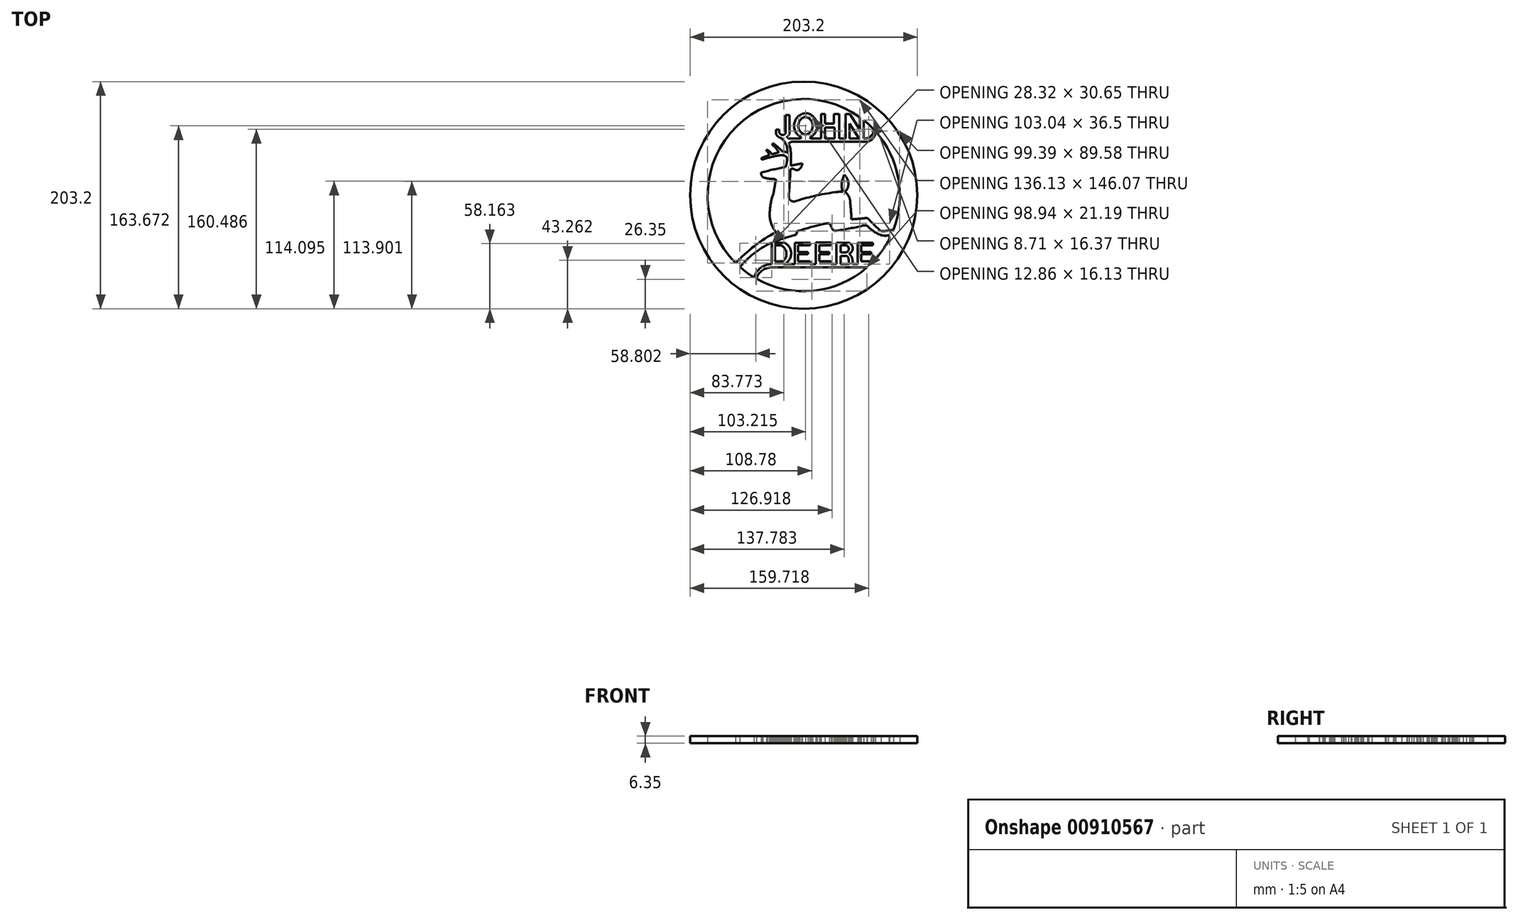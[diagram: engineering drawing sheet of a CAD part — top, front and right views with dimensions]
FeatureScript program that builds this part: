
annotation { "Feature Type Name" : "Feature", "Feature Type Description" : "" }
export const myFeature = defineFeature(function(context is Context, id is Id, definition is map)
    precondition{}
    {
        {
            var Q0;
            Q0=qCreatedBy(makeId("Top.planeOp"),FACE);
            var sketch = newSketch(context, id + "F0", { "sketchPlane" : qUnion([Q0])});
            skCircle(sketch, "E0", {"center": v(101.6, 101.6) * mm, "radius": 101.6 * mm});
            skPoint(sketch, "E0.centerSnap0", {"position": v(0, 101.6) * mm});
            skPoint(sketch, "E0.centerSnap1", {"position": v(101.6, 0) * mm});
            skCircle(sketch, "E1", {"center": v(101.6, 101.6) * mm, "radius": 85.96 * mm});
            skArc(sketch, "E2", {"start": v(76.83, 68.48) * mm, "mid": v(57.67, 56.15) * mm, "end": v(40.77, 40.87) * mm});
            skArc(sketch, "E3", {"start": v(71.8, 58.56) * mm, "mid": v(57.04, 49.4) * mm, "end": v(44.64, 37.22) * mm});
            skArc(sketch, "E4", {"start": v(94.74, 66.06) * mm, "mid": v(86.2, 63.73) * mm, "end": v(77.86, 60.78) * mm});
            skArc(sketch, "E5", {"start": v(71.2, 84.1) * mm, "mid": v(72.6, 75.78) * mm, "end": v(76.83, 68.48) * mm});
            skArc(sketch, "E6", {"start": v(74.65, 103.27) * mm, "mid": v(72.06, 93.84) * mm, "end": v(71.2, 84.1) * mm});
            skArc(sketch, "E7", {"start": v(76.83, 115.22) * mm, "mid": v(75.65, 109.26) * mm, "end": v(74.65, 103.27) * mm});
            skArc(sketch, "E8", {"start": v(76.83, 115.22) * mm, "mid": v(75.85, 115.9) * mm, "end": v(74.65, 115.9) * mm});
            skArc(sketch, "E9", {"start": v(65.1, 117.6) * mm, "mid": v(69.81, 116.4) * mm, "end": v(74.65, 115.9) * mm});
            skArc(sketch, "E10", {"start": v(63.55, 121.74) * mm, "mid": v(63.88, 119.5) * mm, "end": v(65.1, 117.6) * mm});
            skArc(sketch, "E11", {"start": v(85.15, 126.7) * mm, "mid": v(74.28, 124.5) * mm, "end": v(63.55, 121.74) * mm});
            skArc(sketch, "E12", {"start": v(85.15, 126.7) * mm, "mid": v(86.52, 130.95) * mm, "end": v(86.51, 135.41) * mm});
            skArc(sketch, "E13", {"start": v(86.51, 135.41) * mm, "mid": v(83.76, 137.18) * mm, "end": v(80.5, 137.28) * mm});
            skArc(sketch, "E14", {"start": v(80.5, 137.28) * mm, "mid": v(72.72, 135.77) * mm, "end": v(65.1, 133.59) * mm});
            skArc(sketch, "E15", {"start": v(70.75, 137.28) * mm, "mid": v(67.41, 136.16) * mm, "end": v(64.14, 134.86) * mm});
            skArc(sketch, "E16", {"start": v(79.18, 139.83) * mm, "mid": v(76.2, 139.04) * mm, "end": v(73.25, 138.1) * mm});
            skArc(sketch, "E17", {"start": v(87.29, 139.6) * mm, "mid": v(84.96, 140.45) * mm, "end": v(82.5, 140.74) * mm});
            skArc(sketch, "E18", {"start": v(70.75, 137.28) * mm, "mid": v(69.91, 139.5) * mm, "end": v(68.24, 141.2) * mm});
            skArc(sketch, "E19", {"start": v(73.25, 138.1) * mm, "mid": v(71.5, 140.27) * mm, "end": v(69.33, 142.02) * mm});
            skArc(sketch, "E20", {"start": v(79.18, 139.83) * mm, "mid": v(76.9, 143.39) * mm, "end": v(73.94, 146.4) * mm});
            skArc(sketch, "E21", {"start": v(82.5, 140.74) * mm, "mid": v(78.7, 144.39) * mm, "end": v(74.65, 147.76) * mm});
            skArc(sketch, "E22", {"start": v(87.29, 139.6) * mm, "mid": v(85.92, 146.82) * mm, "end": v(81.55, 152.73) * mm});
            skArc(sketch, "E23", {"start": v(90.07, 139.01) * mm, "mid": v(88.79, 146.15) * mm, "end": v(84.7, 152.14) * mm});
            skArc(sketch, "E24", {"start": v(90.07, 127.98) * mm, "mid": v(90.2, 133.5) * mm, "end": v(90.07, 139.01) * mm});
            skArc(sketch, "E25", {"start": v(100.32, 129.94) * mm, "mid": v(95.18, 129.07) * mm, "end": v(90.07, 127.98) * mm});
            skArc(sketch, "E26", {"start": v(96.77, 124.1) * mm, "mid": v(99.29, 126.57) * mm, "end": v(100.32, 129.94) * mm});
            skArc(sketch, "E27", {"start": v(92.71, 125.02) * mm, "mid": v(94.64, 124.13) * mm, "end": v(96.77, 124.1) * mm});
            skArc(sketch, "E28", {"start": v(92.71, 125.02) * mm, "mid": v(91.1, 125.2) * mm, "end": v(89.63, 124.49) * mm});
            skArc(sketch, "E29", {"start": v(88.5, 104.49) * mm, "mid": v(89.22, 114.48) * mm, "end": v(89.63, 124.49) * mm});
            skArc(sketch, "E30", {"start": v(88.5, 104.49) * mm, "mid": v(88.4, 101.57) * mm, "end": v(88.5, 98.65) * mm});
            skArc(sketch, "E31", {"start": v(88.5, 98.65) * mm, "mid": v(91.3, 96.14) * mm, "end": v(95.06, 96.47) * mm});
            skArc(sketch, "E32", {"start": v(131.98, 104.49) * mm, "mid": v(113.33, 101.34) * mm, "end": v(95.06, 96.47) * mm});
            skArc(sketch, "E33", {"start": v(136.48, 104.79) * mm, "mid": v(134.23, 104.64) * mm, "end": v(131.98, 104.49) * mm});
            skArc(sketch, "E34", {"start": v(137.93, 119.83) * mm, "mid": v(135.67, 112.45) * mm, "end": v(136.48, 104.79) * mm});
            skArc(sketch, "E35", {"start": v(141.53, 110.71) * mm, "mid": v(140.82, 115.7) * mm, "end": v(137.93, 119.83) * mm});
            skArc(sketch, "E36", {"start": v(139.3, 105.52) * mm, "mid": v(140.85, 107.93) * mm, "end": v(141.53, 110.71) * mm});
            skArc(sketch, "E37", {"start": v(139.3, 105.52) * mm, "mid": v(139.23, 104.3) * mm, "end": v(139.89, 103.27) * mm});
            skArc(sketch, "E38", {"start": v(143.09, 96.97) * mm, "mid": v(142.03, 100.4) * mm, "end": v(139.89, 103.27) * mm});
            skArc(sketch, "E39", {"start": v(144.4, 79.99) * mm, "mid": v(143.82, 88.49) * mm, "end": v(143.09, 96.97) * mm});
            skArc(sketch, "E40", {"start": v(144.4, 79.99) * mm, "mid": v(151.45, 80.46) * mm, "end": v(158.46, 81.3) * mm});
            skArc(sketch, "E41", {"start": v(158.46, 81.3) * mm, "mid": v(164.51, 75.18) * mm, "end": v(170.8, 69.3) * mm});
            skArc(sketch, "E42", {"start": v(170.8, 69.3) * mm, "mid": v(173.77, 69.49) * mm, "end": v(176.72, 69.88) * mm});
            skArc(sketch, "E43", {"start": v(168.8, 66.67) * mm, "mid": v(173.2, 65.44) * mm, "end": v(177.75, 65.63) * mm});
            skArc(sketch, "E44", {"start": v(158.46, 74.3) * mm, "mid": v(163.23, 69.94) * mm, "end": v(168.8, 66.67) * mm});
            skArc(sketch, "E45", {"start": v(158.46, 74.3) * mm, "mid": v(155.8, 74.57) * mm, "end": v(153.2, 73.99) * mm});
            skArc(sketch, "E46", {"start": v(129.98, 69.6) * mm, "mid": v(141.64, 71.56) * mm, "end": v(153.2, 73.99) * mm});
            skArc(sketch, "E47", {"start": v(126.93, 72.05) * mm, "mid": v(128.02, 70.28) * mm, "end": v(129.98, 69.6) * mm});
            skArc(sketch, "E48", {"start": v(124.63, 76.41) * mm, "mid": v(125.76, 74.22) * mm, "end": v(126.93, 72.05) * mm});
            skArc(sketch, "E49", {"start": v(124.63, 76.41) * mm, "mid": v(120.53, 76.1) * mm, "end": v(116.54, 75.15) * mm});
            skArc(sketch, "E50", {"start": v(116.54, 75.15) * mm, "mid": v(106.19, 72.38) * mm, "end": v(95.92, 69.3) * mm});
            skLineSegment(sketch, "E51", {"start": v(95.92, 69.3) * mm, "end": v(94.74, 66.06) * mm});
            skArc(sketch, "E52", {"start": v(64.14, 134.86) * mm, "mid": v(64.08, 133.82) * mm, "end": v(65.1, 133.59) * mm});
            skArc(sketch, "E53", {"start": v(69.33, 142.02) * mm, "mid": v(68.46, 142.05) * mm, "end": v(68.24, 141.2) * mm});
            skArc(sketch, "E54", {"start": v(74.65, 147.76) * mm, "mid": v(73.79, 147.34) * mm, "end": v(73.94, 146.4) * mm});
            skLineSegment(sketch, "E55", {"start": v(72.96, 58.59) * mm, "end": v(72.96, 39.91) * mm});
            skLineSegment(sketch, "E56", {"start": v(72.96, 39.91) * mm, "end": v(84.43, 39.91) * mm});
            skLineSegment(sketch, "E57", {"start": v(75.4, 59.05) * mm, "end": v(84.3, 59.05) * mm});
            skLineSegment(sketch, "E58", {"start": v(75.92, 56.7) * mm, "end": v(75.92, 42.28) * mm});
            skLineSegment(sketch, "E59", {"start": v(75.92, 42.28) * mm, "end": v(83.2, 42.28) * mm});
            skLineSegment(sketch, "E60", {"start": v(75.92, 56.7) * mm, "end": v(81.54, 56.7) * mm});
            skLineSegment(sketch, "E61", {"start": v(93.6, 59.05) * mm, "end": v(93.6, 39.91) * mm});
            skLineSegment(sketch, "E62", {"start": v(93.6, 39.91) * mm, "end": v(161.47, 39.91) * mm});
            skLineSegment(sketch, "E63", {"start": v(93.6, 59.05) * mm, "end": v(107.18, 59.05) * mm});
            skLineSegment(sketch, "E64", {"start": v(107.18, 59.05) * mm, "end": v(107.18, 56.8) * mm});
            skLineSegment(sketch, "E65", {"start": v(107.18, 56.8) * mm, "end": v(96.62, 56.8) * mm});
            skLineSegment(sketch, "E66", {"start": v(96.62, 56.8) * mm, "end": v(96.62, 50.66) * mm});
            skLineSegment(sketch, "E67", {"start": v(96.62, 50.66) * mm, "end": v(105.52, 50.66) * mm});
            skLineSegment(sketch, "E68", {"start": v(105.52, 50.66) * mm, "end": v(105.52, 48.65) * mm});
            skLineSegment(sketch, "E69", {"start": v(105.52, 48.65) * mm, "end": v(96.62, 48.65) * mm});
            skLineSegment(sketch, "E70", {"start": v(96.62, 48.65) * mm, "end": v(96.62, 42.27) * mm});
            skLineSegment(sketch, "E71", {"start": v(96.62, 42.27) * mm, "end": v(107.18, 42.27) * mm});
            skLineSegment(sketch, "E72", {"start": v(107.18, 42.27) * mm, "end": v(107.18, 39.91) * mm});
            skLineSegment(sketch, "E73", {"start": v(112.5, 59.11) * mm, "end": v(112.5, 39.91) * mm});
            skLineSegment(sketch, "E74", {"start": v(112.5, 59.11) * mm, "end": v(126.08, 59.11) * mm});
            skLineSegment(sketch, "E75", {"start": v(126.08, 59.11) * mm, "end": v(126.08, 56.87) * mm});
            skLineSegment(sketch, "E76", {"start": v(126.08, 56.87) * mm, "end": v(115.52, 56.87) * mm});
            skLineSegment(sketch, "E77", {"start": v(115.52, 56.87) * mm, "end": v(115.52, 50.72) * mm});
            skLineSegment(sketch, "E78", {"start": v(115.52, 50.72) * mm, "end": v(124.42, 50.72) * mm});
            skLineSegment(sketch, "E79", {"start": v(124.42, 50.72) * mm, "end": v(124.42, 48.71) * mm});
            skLineSegment(sketch, "E80", {"start": v(124.42, 48.71) * mm, "end": v(115.52, 48.71) * mm});
            skLineSegment(sketch, "E81", {"start": v(115.52, 48.71) * mm, "end": v(115.52, 42.34) * mm});
            skLineSegment(sketch, "E82", {"start": v(115.52, 42.34) * mm, "end": v(126.08, 42.34) * mm});
            skLineSegment(sketch, "E83", {"start": v(126.08, 42.34) * mm, "end": v(126.08, 39.91) * mm});
            skLineSegment(sketch, "E84", {"start": v(149.94, 59.05) * mm, "end": v(149.94, 39.91) * mm});
            skLineSegment(sketch, "E85", {"start": v(149.94, 59.05) * mm, "end": v(163.52, 59.05) * mm});
            skLineSegment(sketch, "E86", {"start": v(163.52, 59.05) * mm, "end": v(163.52, 56.8) * mm});
            skLineSegment(sketch, "E87", {"start": v(163.52, 56.8) * mm, "end": v(152.96, 56.8) * mm});
            skLineSegment(sketch, "E88", {"start": v(152.96, 56.8) * mm, "end": v(152.96, 50.66) * mm});
            skLineSegment(sketch, "E89", {"start": v(152.96, 50.66) * mm, "end": v(161.86, 50.66) * mm});
            skLineSegment(sketch, "E90", {"start": v(161.86, 50.66) * mm, "end": v(161.86, 48.65) * mm});
            skLineSegment(sketch, "E91", {"start": v(161.86, 48.65) * mm, "end": v(152.96, 48.65) * mm});
            skLineSegment(sketch, "E92", {"start": v(152.96, 48.65) * mm, "end": v(152.96, 42.27) * mm});
            skLineSegment(sketch, "E93", {"start": v(152.96, 42.27) * mm, "end": v(163.52, 42.27) * mm});
            skLineSegment(sketch, "E94", {"start": v(163.52, 42.27) * mm, "end": v(163.52, 39.91) * mm});
            skLineSegment(sketch, "E95", {"start": v(130.76, 39.91) * mm, "end": v(130.76, 59.08) * mm});
            skLineSegment(sketch, "E96", {"start": v(130.76, 59.08) * mm, "end": v(141.44, 59.08) * mm});
            skLineSegment(sketch, "E97", {"start": v(134.77, 39.91) * mm, "end": v(134.77, 47.25) * mm});
            skLineSegment(sketch, "E98", {"start": v(134.77, 47.25) * mm, "end": v(139.02, 47.25) * mm});
            skLineSegment(sketch, "E99", {"start": v(134.77, 50.52) * mm, "end": v(134.77, 56.72) * mm});
            skLineSegment(sketch, "E100", {"start": v(134.77, 56.72) * mm, "end": v(139.83, 56.72) * mm});
            skLineSegment(sketch, "E101", {"start": v(134.77, 50.52) * mm, "end": v(138.9, 50.52) * mm});
            skArc(sketch, "E102", {"start": v(139.83, 50.46) * mm, "mid": v(141.92, 53.6) * mm, "end": v(139.83, 56.72) * mm});
            skArc(sketch, "E103", {"start": v(142.24, 49.2) * mm, "mid": v(145.47, 54.43) * mm, "end": v(141.44, 59.08) * mm});
            skArc(sketch, "E104", {"start": v(144.7, 45.93) * mm, "mid": v(143.63, 47.68) * mm, "end": v(142.24, 49.2) * mm});
            skArc(sketch, "E105", {"start": v(145.45, 39.91) * mm, "mid": v(145.34, 42.95) * mm, "end": v(144.7, 45.93) * mm});
            skArc(sketch, "E106", {"start": v(142.24, 39.91) * mm, "mid": v(141.98, 42.94) * mm, "end": v(141.44, 45.93) * mm});
            skArc(sketch, "E107", {"start": v(141.44, 45.93) * mm, "mid": v(140.4, 46.9) * mm, "end": v(139.02, 47.25) * mm});
            skArc(sketch, "E108", {"start": v(83.2, 42.28) * mm, "mid": v(86.15, 49.93) * mm, "end": v(81.54, 56.7) * mm});
            skArc(sketch, "E109", {"start": v(84.43, 39.91) * mm, "mid": v(90.4, 49.52) * mm, "end": v(84.3, 59.05) * mm});
            skLineSegment(sketch, "E110", {"start": v(138.9, 50.52) * mm, "end": v(139.83, 50.46) * mm});
            skLineSegment(sketch, "E111", {"start": v(85.53, 173.38) * mm, "end": v(88.86, 173.38) * mm});
            skLineSegment(sketch, "E112", {"start": v(88.86, 173.38) * mm, "end": v(88.86, 156.67) * mm});
            skLineSegment(sketch, "E113", {"start": v(85.53, 173.38) * mm, "end": v(85.53, 157.17) * mm});
            skLineSegment(sketch, "E114", {"start": v(76.78, 160.28) * mm, "end": v(79.6, 160.28) * mm});
            skLineSegment(sketch, "E115", {"start": v(79.6, 160.28) * mm, "end": v(79.6, 158.04) * mm});
            skLineSegment(sketch, "E116", {"start": v(76.78, 160.28) * mm, "end": v(76.78, 156.45) * mm});
            skArc(sketch, "E117", {"start": v(76.78, 156.45) * mm, "mid": v(78.71, 154) * mm, "end": v(81.55, 152.73) * mm});
            skArc(sketch, "E118", {"start": v(79.6, 158.04) * mm, "mid": v(82.26, 155.51) * mm, "end": v(85.53, 157.17) * mm});
            skArc(sketch, "E119", {"start": v(103.14, 175.02) * mm, "mid": v(92.98, 163.59) * mm, "end": v(103.23, 152.23) * mm});
            skArc(sketch, "E120", {"start": v(103.23, 152.23) * mm, "mid": v(113.75, 163.67) * mm, "end": v(103.14, 175.02) * mm});
            skArc(sketch, "E121", {"start": v(103.23, 171.74) * mm, "mid": v(96.79, 163.67) * mm, "end": v(103.23, 155.6) * mm});
            skArc(sketch, "E122", {"start": v(103.23, 155.6) * mm, "mid": v(109.64, 163.67) * mm, "end": v(103.23, 171.74) * mm});
            skLineSegment(sketch, "E123", {"start": v(84.7, 152.14) * mm, "end": v(155.36, 152.38) * mm});
            skLineSegment(sketch, "E124", {"start": v(155.36, 152.38) * mm, "end": v(155.36, 168.67) * mm});
            skLineSegment(sketch, "E125", {"start": v(151.84, 171.35) * mm, "end": v(151.84, 160.16) * mm});
            skLineSegment(sketch, "E126", {"start": v(151.84, 160.16) * mm, "end": v(142.97, 174.1) * mm});
            skLineSegment(sketch, "E127", {"start": v(142.97, 174.1) * mm, "end": v(138.96, 174.1) * mm});
            skLineSegment(sketch, "E128", {"start": v(138.96, 174.1) * mm, "end": v(138.96, 152.32) * mm});
            skLineSegment(sketch, "E129", {"start": v(142.6, 152.34) * mm, "end": v(142.56, 165.63) * mm});
            skLineSegment(sketch, "E130", {"start": v(142.56, 165.63) * mm, "end": v(151.26, 152.37) * mm});
            skLineSegment(sketch, "E131", {"start": v(117.18, 152.25) * mm, "end": v(117.1, 174.2) * mm});
            skLineSegment(sketch, "E132", {"start": v(117.1, 174.2) * mm, "end": v(120.73, 174.21) * mm});
            skLineSegment(sketch, "E133", {"start": v(120.73, 174.21) * mm, "end": v(120.76, 165.63) * mm});
            skLineSegment(sketch, "E134", {"start": v(120.76, 165.63) * mm, "end": v(128.75, 165.66) * mm});
            skLineSegment(sketch, "E135", {"start": v(128.75, 165.66) * mm, "end": v(128.75, 174.21) * mm});
            skLineSegment(sketch, "E136", {"start": v(128.75, 174.21) * mm, "end": v(133.4, 174.23) * mm});
            skLineSegment(sketch, "E137", {"start": v(133.4, 174.23) * mm, "end": v(133.47, 152.3) * mm});
            skLineSegment(sketch, "E138", {"start": v(129.3, 152.3) * mm, "end": v(129.3, 162.26) * mm});
            skLineSegment(sketch, "E139", {"start": v(129.3, 162.26) * mm, "end": v(120.73, 162.23) * mm});
            skLineSegment(sketch, "E140", {"start": v(120.73, 162.23) * mm, "end": v(120.77, 152.26) * mm});
            skArc(sketch, "E141", {"start": v(84.77, 152.92) * mm, "mid": v(87.32, 154.24) * mm, "end": v(88.86, 156.67) * mm});
            skArc(sketch, "E142", {"start": v(86.77, 153.8) * mm, "mid": v(87.54, 152.65) * mm, "end": v(88.83, 152.15) * mm});
            skArc(sketch, "E143", {"start": v(98.16, 152.18) * mm, "mid": v(98.94, 152.65) * mm, "end": v(99.66, 153.22) * mm});
            skArc(sketch, "E144", {"start": v(107.1, 153.25) * mm, "mid": v(107.67, 152.6) * mm, "end": v(108.43, 152.22) * mm});
            skPoint(sketch, "E145.endSnap0", {"position": v(88.32, 150.38) * mm});
            skLineSegment(sketch, "E146", {"start": v(155.36, 150.38) * mm, "end": v(155.36, 152.38) * mm});
            skArc(sketch, "E147", {"start": v(91.96, 149.45) * mm, "mid": v(89.83, 148.98) * mm, "end": v(88.09, 147.65) * mm});
            skLineSegment(sketch, "E148", {"start": v(91.96, 149.45) * mm, "end": v(157.05, 149.33) * mm});
            skArc(sketch, "E149", {"start": v(157.05, 149.33) * mm, "mid": v(163.5, 152.19) * mm, "end": v(165.7, 158.88) * mm});
            skArc(sketch, "E150", {"start": v(155.36, 152.38) * mm, "mid": v(161.77, 154.35) * mm, "end": v(164.07, 160.65) * mm});
            skArc(sketch, "E151", {"start": v(75.4, 59.05) * mm, "mid": v(76.64, 59.9) * mm, "end": v(77.86, 60.78) * mm});
            skLineSegment(sketch, "E152", {"start": v(72.96, 58.59) * mm, "end": v(71.8, 58.56) * mm});
            skLineSegment(sketch, "E153", {"start": v(93.6, 39.91) * mm, "end": v(84.43, 39.91) * mm});
            skLineSegment(sketch, "E154", {"start": v(158.25, 36.95) * mm, "end": v(72.96, 36.95) * mm});
            skLineSegment(sketch, "E155", {"start": v(72.96, 36.95) * mm, "end": v(72.96, 39.91) * mm});
            skArc(sketch, "E156", {"start": v(72.96, 39.91) * mm, "mid": v(63.1, 36.58) * mm, "end": v(57.3, 27.94) * mm});
            skArc(sketch, "E157", {"start": v(72.96, 36.95) * mm, "mid": v(64.45, 34.12) * mm, "end": v(59.31, 26.76) * mm});
            skLineSegment(sketch, "E158", {"start": v(177.75, 65.63) * mm, "end": v(178.44, 63.06) * mm});
            skLineSegment(sketch, "E159", {"start": v(176.72, 69.88) * mm, "end": v(181.83, 70.75) * mm});
            skSolve(sketch);
        }
        {
            var Q0;
            {var subQ7=sQuery(id+"F0.wireOp",EDGE,"E2");Q0=makeQuery(id+"F0.imprint","IMPRINT",FACE,{"disambiguationData":[TD([[makeQuery(id+"F0.imprint","IMPRINT",EDGE,{"derivedFrom":subQ7}),1.0]])]});}
            var Q1;
            {var subQ1=sQuery(id+"F0.wireOp",EDGE,"E61");Q1=makeQuery(id+"F0.imprint","IMPRINT",FACE,{"disambiguationData":[TD([[makeQuery(id+"F0.imprint","IMPRINT",EDGE,{"derivedFrom":subQ1}),1.0]])]});}
            var Q2;
            {var subQ0=sQuery(id+"F0.wireOp",EDGE,"E73");Q2=makeQuery(id+"F0.imprint","IMPRINT",FACE,{"disambiguationData":[TD([[makeQuery(id+"F0.imprint","IMPRINT",EDGE,{"derivedFrom":subQ0}),1.0]])]});}
            var Q3;
            {var subQ1=sQuery(id+"F0.wireOp",EDGE,"E95");Q3=makeQuery(id+"F0.imprint","IMPRINT",FACE,{"disambiguationData":[TD([[makeQuery(id+"F0.imprint","IMPRINT",EDGE,{"derivedFrom":subQ1}),-1.0]])]});}
            var Q4;
            {var subQ5=sQuery(id+"F0.wireOp",EDGE,"E84");Q4=makeQuery(id+"F0.imprint","IMPRINT",FACE,{"disambiguationData":[TD([[makeQuery(id+"F0.imprint","IMPRINT",EDGE,{"derivedFrom":subQ5}),1.0]])]});}
            var Q5;
            Q5=makeQuery(id+"F0.imprint","IMPRINT",FACE,{"disambiguationData":[TD([[makeQuery(id+"F0.imprint","IMPRINT",EDGE,{"derivedFrom":sQuery(id+"F0.wireOp",EDGE,"E56")}),-1.0]])]});
            var Q6;
            Q6=makeQuery(id+"F0.imprint","IMPRINT",FACE,{"disambiguationData":[TD([[makeQuery(id+"F0.imprint","IMPRINT",EDGE,{"derivedFrom":sQuery(id+"F0.wireOp",EDGE,"E0")}),1.0]])]});
            var Q7;
            Q7=makeQuery(id+"F0.imprint","IMPRINT",FACE,{"disambiguationData":[TD([[makeQuery(id+"F0.imprint","IMPRINT",EDGE,{"derivedFrom":sQuery(id+"F0.wireOp",EDGE,"E155")}),1.0]])]});
            var Q8;
            {var subQ7=sQuery(id+"F0.wireOp",EDGE,"E147");Q8=makeQuery(id+"F0.imprint","IMPRINT",FACE,{"disambiguationData":[TD([[makeQuery(id+"F0.imprint","IMPRINT",EDGE,{"derivedFrom":subQ7}),-1.0]])]});}
            var Q9;
            {var subQ0=sQuery(id+"F0.wireOp",EDGE,"E143");Q9=makeQuery(id+"F0.imprint","IMPRINT",FACE,{"disambiguationData":[TD([[makeQuery(id+"F0.imprint","IMPRINT",EDGE,{"derivedFrom":subQ0}),-1.0]])]});}
            var Q10;
            Q10=makeQuery(id+"F0.imprint","IMPRINT",FACE,{"disambiguationData":[TD([[makeQuery(id+"F0.imprint","IMPRINT",EDGE,{"derivedFrom":sQuery(id+"F0.wireOp",EDGE,"E121")}),-1.0]])]});
            var Q11;
            {var subQ2=sQuery(id+"F0.wireOp",EDGE,"E131");Q11=makeQuery(id+"F0.imprint","IMPRINT",FACE,{"disambiguationData":[TD([[makeQuery(id+"F0.imprint","IMPRINT",EDGE,{"derivedFrom":subQ2}),-1.0]])]});}
            var Q12;
            {var subQ0=sQuery(id+"F0.wireOp",EDGE,"E124");Q12=makeQuery(id+"F0.imprint","IMPRINT",FACE,{"disambiguationData":[TD([[makeQuery(id+"F0.imprint","IMPRINT",EDGE,{"derivedFrom":subQ0}),1.0]])]});}
            extrude(context, id + "F1", {"entities" : qUnion([Q0, Q1, Q2, Q3, Q4, Q5, Q6, Q7, Q8, Q9, Q10, Q11, Q12]), "depth" : 6.35 * mm, "offsetDistance" : 25.4 * mm});
        }
    });
